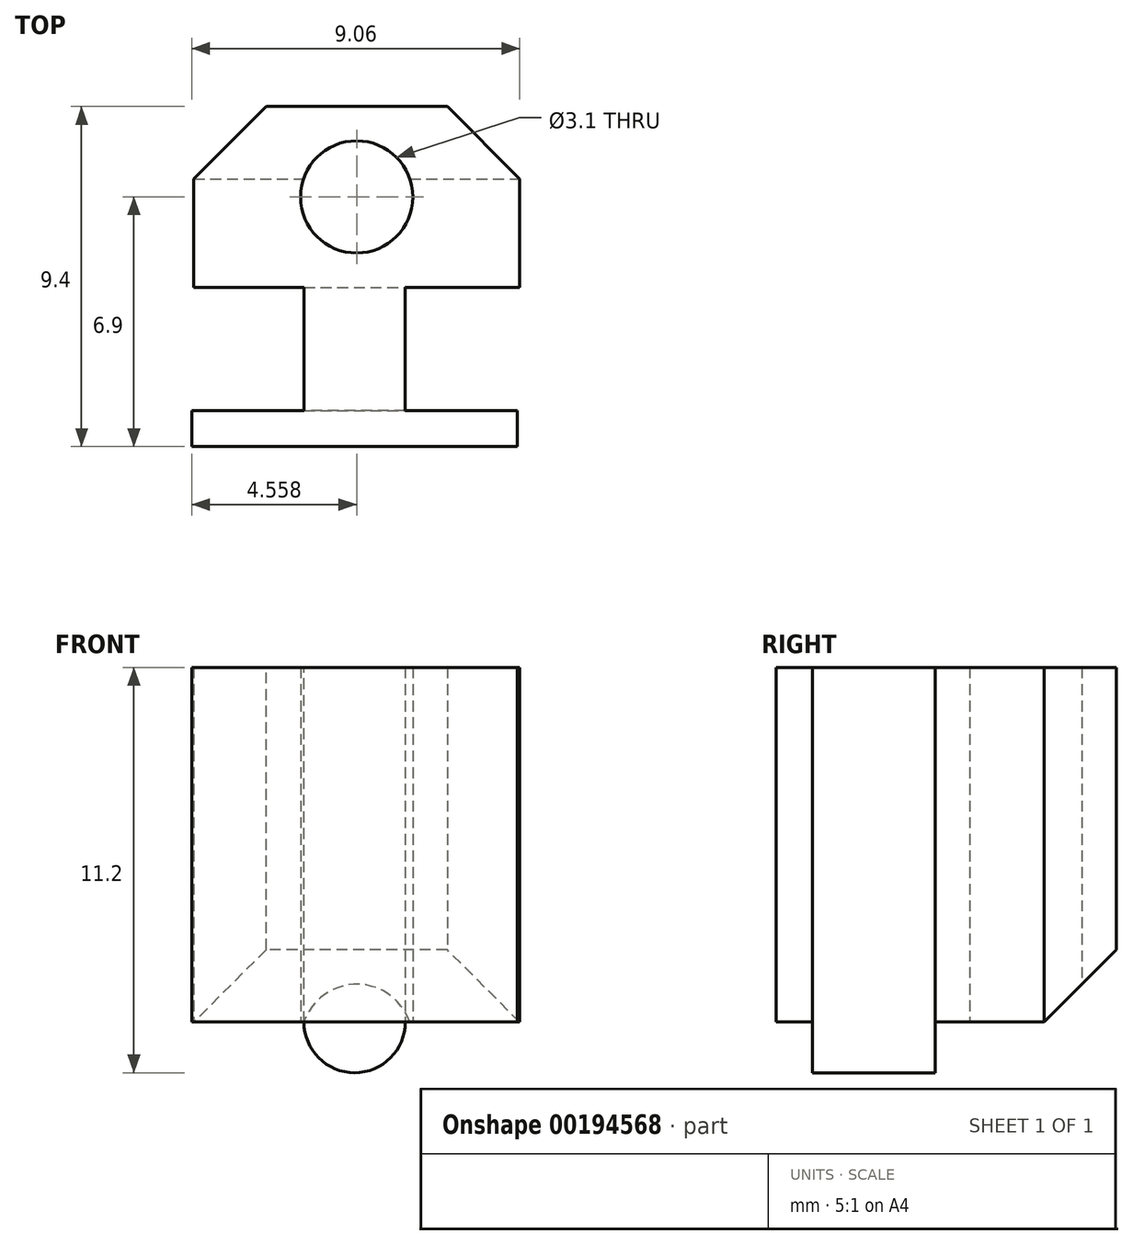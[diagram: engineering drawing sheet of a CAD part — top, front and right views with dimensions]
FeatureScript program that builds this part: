
annotation { "Feature Type Name" : "Feature", "Feature Type Description" : "" }
export const myFeature = defineFeature(function(context is Context, id is Id, definition is map)
    precondition{}
    {
        {
            var Q0;
            Q0=qCreatedBy(makeId("Front.planeOp"),FACE);
            var sketch = newSketch(context, id + "F0", { "sketchPlane" : qUnion([Q0])});
            skLineSegment(sketch, "E0", {"start": v(0, 0) * mm, "end": v(2.8, 0) * mm});
            skLineSegment(sketch, "E1", {"start": v(2.8, 0) * mm, "end": v(2.8, -9.8) * mm});
            skLineSegment(sketch, "E2", {"start": v(0, -9.8) * mm, "end": v(0, 0) * mm});
            skArc(sketch, "E3", {"start": v(0, -9.8) * mm, "mid": v(1.4, -11.2) * mm, "end": v(2.8, -9.8) * mm});
            skSolve(sketch);
        }
        {
            var Q0;
            Q0 = qSketchRegion(id + "F0", true);
            extrude(context, id + "F1", {"entities" : qUnion([Q0]), "depth" : 3.4 * mm});
        }
        {
            var Q0;
            Q0=makeQuery(id+"F1.opExtrude","CAP_FACE",FACE,{"disambiguationData":[OSD([sQuery(id+"F0.wireOp",EDGE,"E0"),sQuery(id+"F0.wireOp",EDGE,"E1"),sQuery(id+"F0.wireOp",EDGE,"E2"),sQuery(id+"F0.wireOp",EDGE,"E3")])],"isStart":false});
            var sketch = newSketch(context, id + "F2", { "sketchPlane" : qUnion([Q0])});
            skLineSegment(sketch, "E4", {"start": v(-3.1, 0) * mm, "end": v(5.9, 0) * mm});
            skLineSegment(sketch, "E5", {"start": v(5.9, 0) * mm, "end": v(5.9, -9.8) * mm});
            skLineSegment(sketch, "E6", {"start": v(5.9, -9.8) * mm, "end": v(-3.1, -9.8) * mm});
            skLineSegment(sketch, "E7", {"start": v(-3.1, -9.8) * mm, "end": v(-3.1, 0) * mm});
            skLineSegment(sketch, "E8", {"start": v(1.4, 0) * mm, "end": v(1.4, 0.86) * mm, "construction": true});
            skSolve(sketch);
        }
        {
            var Q0;
            Q0 = qSketchRegion(id + "F2", true);
            extrude(context, id + "F3", {"entities" : qUnion([Q0]), "operationType" : NewBodyOperationType.ADD, "depth" : 1 * mm});
        }
        {
            var Q0;
            Q0=makeQuery(id+"F1.opExtrude","CAP_FACE",FACE,{"disambiguationData":[OSD([sQuery(id+"F0.wireOp",EDGE,"E0"),sQuery(id+"F0.wireOp",EDGE,"E1"),sQuery(id+"F0.wireOp",EDGE,"E2"),sQuery(id+"F0.wireOp",EDGE,"E3")])],"isStart":true});
            var sketch = newSketch(context, id + "F4", { "sketchPlane" : qUnion([Q0])});
            skLineSegment(sketch, "E9", {"start": v(-5.96, 0) * mm, "end": v(3.04, 0) * mm});
            skLineSegment(sketch, "E10", {"start": v(3.04, 0) * mm, "end": v(3.04, -9.8) * mm});
            skLineSegment(sketch, "E11", {"start": v(3.04, -9.8) * mm, "end": v(-5.96, -9.8) * mm});
            skLineSegment(sketch, "E12", {"start": v(-5.96, 0) * mm, "end": v(-5.96, -9.8) * mm});
            skSolve(sketch);
        }
        {
            var Q0;
            Q0 = qSketchRegion(id + "F4", true);
            extrude(context, id + "F5", {"entities" : qUnion([Q0]), "operationType" : NewBodyOperationType.ADD, "depth" : 5 * mm});
        }
        {
            var Q0;
            Q0=makeQuery(id+"F5.boolean.opBoolean","MERGE",FACE,{"derivedFrom":[makeQuery(id+"F3.boolean.opBoolean","MERGE",FACE,{"derivedFrom":[makeQuery(id+"F1.opExtrude","SWEPT_FACE",FACE,{"disambiguationData":[OSD([sQuery(id+"F0.wireOp",EDGE,"E0")])]}),makeQuery(id+"F3.opExtrude","SWEPT_FACE",FACE,{"disambiguationData":[OSD([sQuery(id+"F2.wireOp",EDGE,"E4")])]})]}),makeQuery(id+"F5.opExtrude","SWEPT_FACE",FACE,{"disambiguationData":[OSD([sQuery(id+"F4.wireOp",EDGE,"E9")])]})]});
            var sketch = newSketch(context, id + "F6", { "sketchPlane" : qUnion([Q0])});
            skPoint(sketch, "E13", {"position": v(1.46, 2.5) * mm});
            skPoint(sketch, "E13.positionSnap0", {"position": v(1.46, 5) * mm});
            skPoint(sketch, "E13.positionSnap1", {"position": v(5.96, 2.5) * mm});
            skSolve(sketch);
        }
        {
            var Q0;
            Q0=sQuery(id+"F6.wireOp",VERTEX,"E13");
            var Q1;
            Q1=makeQuery(id+"F1.opExtrude","SWEPT_BODY",BODY,{"disambiguationData":[OSD([sQuery(id+"F0.wireOp",EDGE,"E0"),sQuery(id+"F0.wireOp",EDGE,"E1"),sQuery(id+"F0.wireOp",EDGE,"E2"),sQuery(id+"F0.wireOp",EDGE,"E3")])]});
            hole(context, id + "F7", {"style" : HoleStyle.SIMPLE, "endStyle" : HoleEndStyle.THROUGH, "holeDiameter" : 3.1 * mm, "locations" : qUnion([Q0]), "scope" : qUnion([Q1]), "isTappedThrough" : true, "startStyle" : HoleStartStyle.SKETCH});
        }
        {
            var Q0;
            Q0=makeQuery(id+"F5.opExtrude","CAP_EDGE",EDGE,{"disambiguationData":[OSD([sQuery(id+"F4.wireOp",EDGE,"E10")])],"isStart":false});
            var Q1;
            Q1=makeQuery(id+"F5.opExtrude","CAP_EDGE",EDGE,{"disambiguationData":[OSD([sQuery(id+"F4.wireOp",EDGE,"E12")])],"isStart":false});
            var Q2;
            Q2=makeQuery(id+"F5.opExtrude","CAP_EDGE",EDGE,{"disambiguationData":[OSD([sQuery(id+"F4.wireOp",EDGE,"E11")])],"isStart":false});
            chamfer(context, id + "F8", {"entities" : qUnion([Q0, Q1, Q2]), "width" : 2 * mm, "tangentPropagation" : true});
        }
    });
